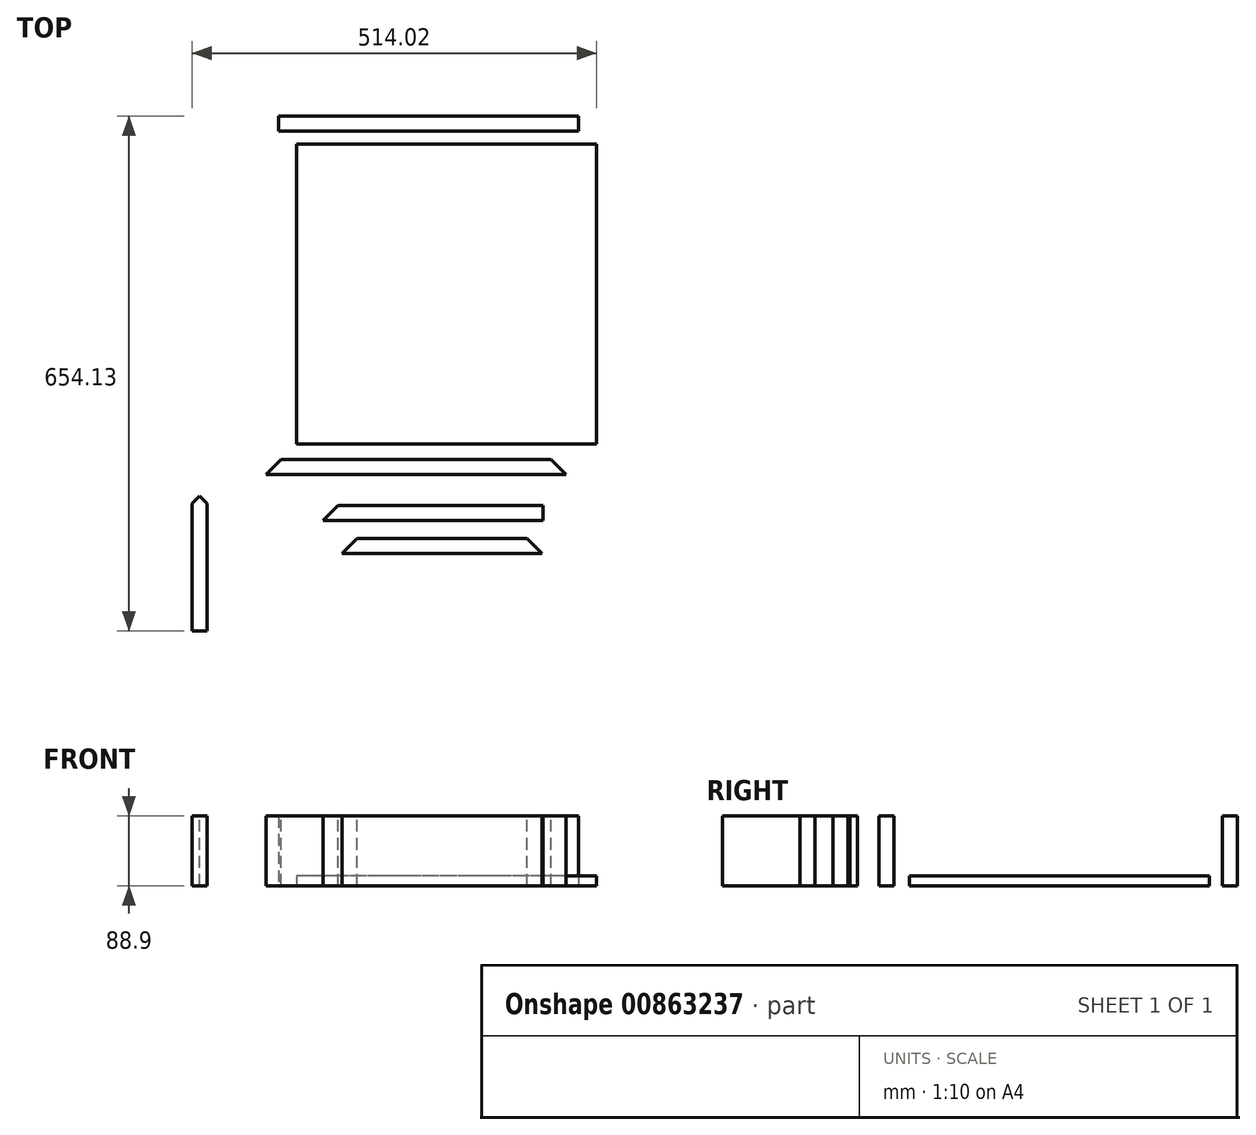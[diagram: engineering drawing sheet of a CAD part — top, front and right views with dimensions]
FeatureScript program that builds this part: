
annotation { "Feature Type Name" : "Feature", "Feature Type Description" : "" }
export const myFeature = defineFeature(function(context is Context, id is Id, definition is map)
    precondition{}
    {
        {
            var Q0;
            Q0=qCreatedBy(makeId("Top.planeOp"),FACE);
            var sketch = newSketch(context, id + "F0", { "sketchPlane" : qUnion([Q0])});
            skLineSegment(sketch, "E0.bottom", {"start": v(190.5, -190.5) * mm, "end": v(-190.5, -190.5) * mm});
            skLineSegment(sketch, "E0.top", {"start": v(190.5, 190.5) * mm, "end": v(-190.5, 190.5) * mm});
            skLineSegment(sketch, "E0.left", {"start": v(190.5, -190.5) * mm, "end": v(190.5, 190.5) * mm});
            skLineSegment(sketch, "E0.right", {"start": v(-190.5, -190.5) * mm, "end": v(-190.5, 190.5) * mm});
            skPoint(sketch, "E0.middle", {"position": v(0, 0) * mm});
            skSolve(sketch);
        }
        {
            var Q0;
            Q0 = qSketchRegion(id + "F0", true);
            extrude(context, id + "F1", {"entities" : qUnion([Q0]), "depth" : 12.7 * mm, "offsetDistance" : 25.4 * mm});
        }
        {
            var Q0;
            Q0=qCreatedBy(makeId("Top.planeOp"),FACE);
            var sketch = newSketch(context, id + "F2", { "sketchPlane" : qUnion([Q0])});
            skLineSegment(sketch, "E1.bottom", {"start": v(-213.35, 226.1) * mm, "end": v(167.65, 226.1) * mm});
            skLineSegment(sketch, "E1.top", {"start": v(-213.35, 207.06) * mm, "end": v(167.65, 207.06) * mm});
            skLineSegment(sketch, "E1.left", {"start": v(-213.35, 226.1) * mm, "end": v(-213.35, 207.06) * mm});
            skLineSegment(sketch, "E1.right", {"start": v(167.65, 226.1) * mm, "end": v(167.65, 207.06) * mm});
            skSolve(sketch);
        }
        {
            var Q0;
            Q0 = qSketchRegion(id + "F2", true);
            extrude(context, id + "F3", {"entities" : qUnion([Q0]), "depth" : 88.9 * mm, "offsetDistance" : 25.4 * mm});
        }
        {
            var Q0;
            Q0=qCreatedBy(makeId("Top.planeOp"),FACE);
            var sketch = newSketch(context, id + "F4", { "sketchPlane" : qUnion([Q0])});
            skLineSegment(sketch, "E2.bottom", {"start": v(-229.5, -210.43) * mm, "end": v(151.5, -210.43) * mm});
            skLineSegment(sketch, "E2.top", {"start": v(-229.5, -229.48) * mm, "end": v(151.5, -229.48) * mm});
            skLineSegment(sketch, "E2.left", {"start": v(-229.5, -210.43) * mm, "end": v(-229.5, -229.48) * mm});
            skLineSegment(sketch, "E2.right", {"start": v(151.5, -210.43) * mm, "end": v(151.5, -229.48) * mm});
            skSolve(sketch);
        }
        {
            var Q0;
            Q0 = qSketchRegion(id + "F4", true);
            extrude(context, id + "F5", {"entities" : qUnion([Q0]), "depth" : 88.9 * mm, "offsetDistance" : 25.4 * mm});
        }
        {
            var Q0;
            Q0=makeQuery(id+"F5.opExtrude","CAP_FACE",FACE,{"disambiguationData":[OSD([sQuery(id+"F4.wireOp",EDGE,"E2.bottom"),sQuery(id+"F4.wireOp",EDGE,"E2.top"),sQuery(id+"F4.wireOp",EDGE,"E2.left"),sQuery(id+"F4.wireOp",EDGE,"E2.right")])],"isStart":false});
            var sketch = newSketch(context, id + "F6", { "sketchPlane" : qUnion([Q0])});
            skLineSegment(sketch, "E3", {"start": v(-229.5, -210.43) * mm, "end": v(-210.46, -210.43) * mm});
            skLineSegment(sketch, "E4", {"start": v(-210.46, -210.43) * mm, "end": v(-229.5, -229.48) * mm});
            skLineSegment(sketch, "E5", {"start": v(-229.5, -229.48) * mm, "end": v(-229.5, -210.43) * mm});
            skLineSegment(sketch, "E6", {"start": v(151.5, -210.43) * mm, "end": v(132.44, -210.43) * mm});
            skLineSegment(sketch, "E7", {"start": v(132.44, -210.43) * mm, "end": v(151.5, -229.48) * mm});
            skLineSegment(sketch, "E8", {"start": v(151.5, -229.48) * mm, "end": v(151.5, -210.43) * mm});
            skSolve(sketch);
        }
        {
            var Q0;
            Q0 = qSketchRegion(id + "F6", true);
            extrude(context, id + "F7", {"entities" : qUnion([Q0]), "operationType" : NewBodyOperationType.REMOVE, "endBound" : BoundingType.THROUGH_ALL, "oppositeDirection" : true, "depth" : 25.4 * mm, "offsetDistance" : 25.4 * mm});
        }
        {
            var Q0;
            Q0=qCreatedBy(makeId("Top.planeOp"),FACE);
            var sketch = newSketch(context, id + "F8", { "sketchPlane" : qUnion([Q0])});
            skLineSegment(sketch, "E9.bottom", {"start": v(-157.19, -268.53) * mm, "end": v(122.21, -268.53) * mm});
            skLineSegment(sketch, "E9.top", {"start": v(-157.19, -287.58) * mm, "end": v(122.21, -287.58) * mm});
            skLineSegment(sketch, "E9.left", {"start": v(-157.19, -268.53) * mm, "end": v(-157.19, -287.58) * mm});
            skLineSegment(sketch, "E9.right", {"start": v(122.21, -268.53) * mm, "end": v(122.21, -287.58) * mm});
            skSolve(sketch);
        }
        {
            var Q0;
            Q0 = qSketchRegion(id + "F8", true);
            extrude(context, id + "F9", {"entities" : qUnion([Q0]), "depth" : 88.9 * mm, "offsetDistance" : 25.4 * mm});
        }
        {
            var Q0;
            Q0=qCreatedBy(makeId("Top.planeOp"),FACE);
            var sketch = newSketch(context, id + "F10", { "sketchPlane" : qUnion([Q0])});
            skLineSegment(sketch, "E10.bottom", {"start": v(-132.8, -310.76) * mm, "end": v(121.2, -310.76) * mm});
            skLineSegment(sketch, "E10.top", {"start": v(-132.8, -329.8) * mm, "end": v(121.2, -329.8) * mm});
            skLineSegment(sketch, "E10.left", {"start": v(-132.8, -310.76) * mm, "end": v(-132.8, -329.8) * mm});
            skLineSegment(sketch, "E10.right", {"start": v(121.2, -310.76) * mm, "end": v(121.2, -329.8) * mm});
            skSolve(sketch);
        }
        {
            var Q0;
            Q0 = qSketchRegion(id + "F10", true);
            extrude(context, id + "F11", {"entities" : qUnion([Q0]), "depth" : 88.9 * mm, "offsetDistance" : 25.4 * mm});
        }
        {
            var Q0;
            Q0=makeQuery(id+"F9.opExtrude","CAP_FACE",FACE,{"disambiguationData":[OSD([sQuery(id+"F8.wireOp",EDGE,"E9.bottom"),sQuery(id+"F8.wireOp",EDGE,"E9.top"),sQuery(id+"F8.wireOp",EDGE,"E9.left"),sQuery(id+"F8.wireOp",EDGE,"E9.right")])],"isStart":false});
            var sketch = newSketch(context, id + "F12", { "sketchPlane" : qUnion([Q0])});
            skLineSegment(sketch, "E11", {"start": v(-157.19, -268.53) * mm, "end": v(-138.14, -268.53) * mm});
            skLineSegment(sketch, "E12", {"start": v(-138.14, -268.53) * mm, "end": v(-157.19, -287.58) * mm});
            skLineSegment(sketch, "E13", {"start": v(-157.19, -287.58) * mm, "end": v(-157.19, -268.53) * mm});
            skSolve(sketch);
        }
        {
            var Q0;
            Q0 = qSketchRegion(id + "F12", true);
            extrude(context, id + "F13", {"entities" : qUnion([Q0]), "operationType" : NewBodyOperationType.REMOVE, "endBound" : BoundingType.THROUGH_ALL, "oppositeDirection" : true, "depth" : 25.4 * mm, "offsetDistance" : 25.4 * mm});
        }
        {
            var Q0;
            Q0=makeQuery(id+"F11.opExtrude","CAP_FACE",FACE,{"disambiguationData":[OSD([sQuery(id+"F10.wireOp",EDGE,"E10.bottom"),sQuery(id+"F10.wireOp",EDGE,"E10.top"),sQuery(id+"F10.wireOp",EDGE,"E10.left"),sQuery(id+"F10.wireOp",EDGE,"E10.right")])],"isStart":false});
            var sketch = newSketch(context, id + "F14", { "sketchPlane" : qUnion([Q0])});
            skLineSegment(sketch, "E14", {"start": v(-132.8, -329.8) * mm, "end": v(-132.8, -310.76) * mm});
            skLineSegment(sketch, "E15", {"start": v(-132.8, -310.76) * mm, "end": v(-113.75, -310.76) * mm});
            skLineSegment(sketch, "E16", {"start": v(-113.75, -310.76) * mm, "end": v(-132.8, -329.8) * mm});
            skLineSegment(sketch, "E17", {"start": v(102.15, -310.76) * mm, "end": v(121.2, -310.76) * mm});
            skLineSegment(sketch, "E18", {"start": v(121.2, -310.76) * mm, "end": v(121.2, -329.8) * mm});
            skLineSegment(sketch, "E19", {"start": v(121.2, -329.8) * mm, "end": v(102.15, -310.76) * mm});
            skSolve(sketch);
        }
        {
            var Q0;
            Q0 = qSketchRegion(id + "F14", true);
            extrude(context, id + "F15", {"entities" : qUnion([Q0]), "operationType" : NewBodyOperationType.REMOVE, "endBound" : BoundingType.THROUGH_ALL, "oppositeDirection" : true, "depth" : 25.4 * mm, "offsetDistance" : 25.4 * mm});
        }
        {
            var Q0;
            Q0=qCreatedBy(makeId("Top.planeOp"),FACE);
            var sketch = newSketch(context, id + "F16", { "sketchPlane" : qUnion([Q0])});
            skLineSegment(sketch, "E20.bottom", {"start": v(-323.52, -256.57) * mm, "end": v(-304.47, -256.57) * mm});
            skLineSegment(sketch, "E20.top", {"start": v(-323.52, -428.02) * mm, "end": v(-304.47, -428.02) * mm});
            skLineSegment(sketch, "E20.left", {"start": v(-323.52, -256.57) * mm, "end": v(-323.52, -428.02) * mm});
            skLineSegment(sketch, "E20.right", {"start": v(-304.47, -256.57) * mm, "end": v(-304.47, -428.02) * mm});
            skSolve(sketch);
        }
        {
            var Q0;
            Q0 = qSketchRegion(id + "F16", true);
            extrude(context, id + "F17", {"entities" : qUnion([Q0]), "depth" : 88.9 * mm, "offsetDistance" : 25.4 * mm});
        }
        {
            var Q0;
            Q0=makeQuery(id+"F17.opExtrude","CAP_FACE",FACE,{"disambiguationData":[OSD([sQuery(id+"F16.wireOp",EDGE,"E20.bottom"),sQuery(id+"F16.wireOp",EDGE,"E20.top"),sQuery(id+"F16.wireOp",EDGE,"E20.left"),sQuery(id+"F16.wireOp",EDGE,"E20.right")])],"isStart":false});
            var sketch = newSketch(context, id + "F18", { "sketchPlane" : qUnion([Q0])});
            skLineSegment(sketch, "E21", {"start": v(-323.52, -266.1) * mm, "end": v(-314, -256.57) * mm});
            skLineSegment(sketch, "E22", {"start": v(-314, -256.57) * mm, "end": v(-304.47, -266.1) * mm});
            skLineSegment(sketch, "E23", {"start": v(-304.47, -266.1) * mm, "end": v(-323.52, -266.1) * mm});
            skSolve(sketch);
        }
        {
            var Q0;
            {var subQ0=sQuery(id+"F18.wireOp",EDGE,"E21");Q0=makeQuery(id+"F18.imprint","IMPRINT",FACE,{"disambiguationData":[TD([[makeQuery(id+"F18.imprint","IMPRINT",EDGE,{"derivedFrom":subQ0}),1.0]])]});}
            var Q1;
            {var subQ0=sQuery(id+"F18.wireOp",EDGE,"E22");Q1=makeQuery(id+"F18.imprint","IMPRINT",FACE,{"disambiguationData":[TD([[makeQuery(id+"F18.imprint","IMPRINT",EDGE,{"derivedFrom":subQ0}),1.0]])]});}
            extrude(context, id + "F19", {"entities" : qUnion([Q0, Q1]), "operationType" : NewBodyOperationType.REMOVE, "endBound" : BoundingType.THROUGH_ALL, "oppositeDirection" : true, "depth" : 25.4 * mm, "offsetDistance" : 25.4 * mm});
        }
    });
